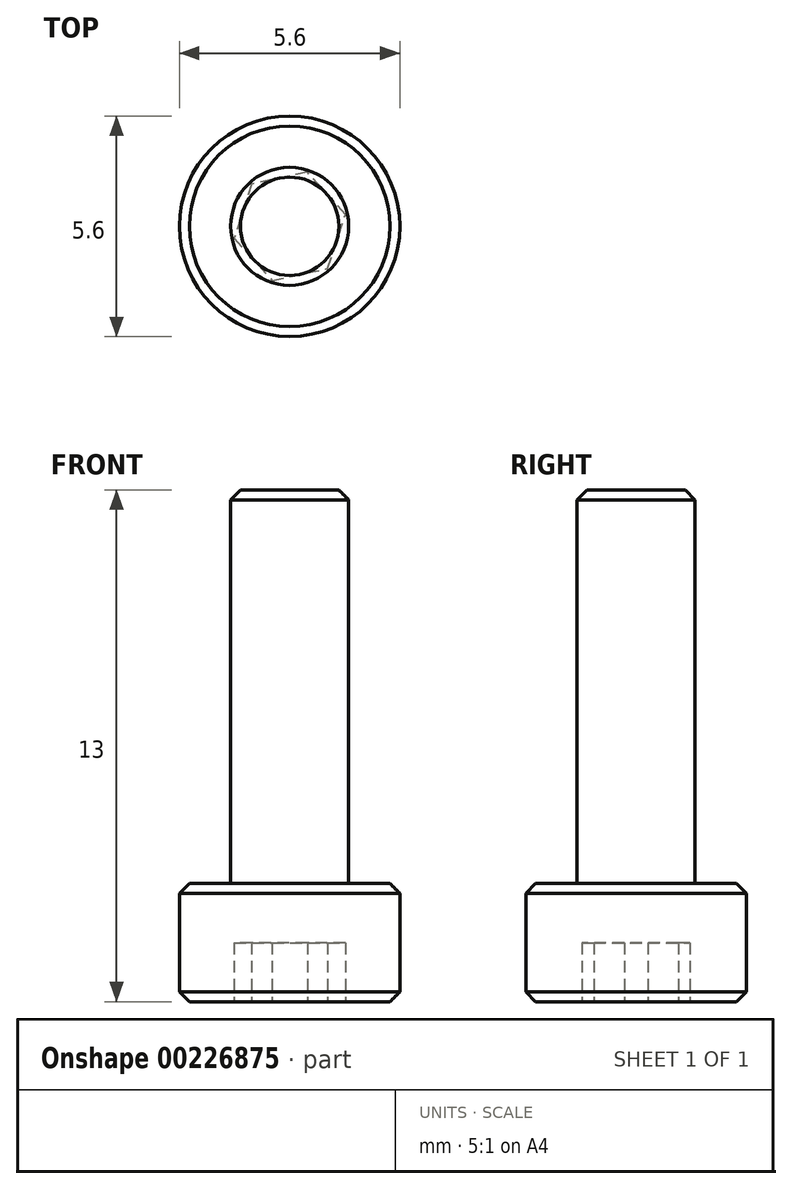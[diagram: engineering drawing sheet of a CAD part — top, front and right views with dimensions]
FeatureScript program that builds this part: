
annotation { "Feature Type Name" : "Feature", "Feature Type Description" : "" }
export const myFeature = defineFeature(function(context is Context, id is Id, definition is map)
    precondition{}
    {
        {
            var Q0;
            Q0=qCreatedBy(makeId("Top.planeOp"),FACE);
            var sketch = newSketch(context, id + "F0", { "sketchPlane" : qUnion([Q0])});
            skCircle(sketch, "E0", {"center": v(0, 0) * mm, "radius": 1.5 * mm});
            skSolve(sketch);
        }
        {
            var Q0;
            Q0 = qSketchRegion(id + "F0", true);
            extrude(context, id + "F1", {"entities" : qUnion([Q0]), "depth" : 10 * mm});
        }
        {
            var Q0;
            Q0=qCreatedBy(makeId("Top.planeOp"),FACE);
            var sketch = newSketch(context, id + "F2", { "sketchPlane" : qUnion([Q0])});
            skCircle(sketch, "E1", {"center": v(0, 0) * mm, "radius": 2.8 * mm});
            skSolve(sketch);
        }
        {
            var Q0;
            Q0 = qSketchRegion(id + "F2", true);
            extrude(context, id + "F3", {"entities" : qUnion([Q0]), "operationType" : NewBodyOperationType.ADD, "oppositeDirection" : true, "depth" : 3 * mm});
        }
        {
            var Q0;
            Q0=makeQuery(id+"F3.opExtrude","CAP_FACE",FACE,{"disambiguationData":[OSD([sQuery(id+"F2.wireOp",EDGE,"E1")])],"isStart":false});
            var sketch = newSketch(context, id + "F4", { "sketchPlane" : qUnion([Q0])});
            skCircle(sketch, "E2.cCircle", {"center": v(0, 0) * mm, "radius": 1.25 * mm, "construction": true});
            skLineSegment(sketch, "E2.0", {"start": v(1.41, -0.3) * mm, "end": v(0.45, -1.37) * mm});
            skLineSegment(sketch, "E2.1", {"start": v(0.45, -1.37) * mm, "end": v(-0.97, -1.07) * mm});
            skLineSegment(sketch, "E2.2", {"start": v(-0.97, -1.07) * mm, "end": v(-1.41, 0.3) * mm});
            skLineSegment(sketch, "E2.3", {"start": v(-1.41, 0.3) * mm, "end": v(-0.45, 1.37) * mm});
            skLineSegment(sketch, "E2.4", {"start": v(-0.45, 1.37) * mm, "end": v(0.97, 1.07) * mm});
            skLineSegment(sketch, "E2.5", {"start": v(0.97, 1.07) * mm, "end": v(1.41, -0.3) * mm});
            skPoint(sketch, "E2.0.midPoint", {"position": v(0.93, -0.84) * mm});
            skSolve(sketch);
        }
        {
            var Q0;
            Q0=makeQuery(id+"F4.imprint","IMPRINT",FACE,{"disambiguationData":[TD([[makeQuery(id+"F4.imprint","IMPRINT",EDGE,{"derivedFrom":sQuery(id+"F4.wireOp",EDGE,"E2.0")}),-1.0]])]});
            extrude(context, id + "F5", {"entities" : qUnion([Q0]), "operationType" : NewBodyOperationType.REMOVE, "oppositeDirection" : true, "depth" : 1.5 * mm});
        }
        {
            var Q0;
            Q0=makeQuery(id+"F3.opExtrude","CAP_EDGE",EDGE,{"disambiguationData":[OSD([sQuery(id+"F2.wireOp",EDGE,"E1")])],"isStart":false});
            var Q1;
            Q1=makeQuery(id+"F1.opExtrude","CAP_EDGE",EDGE,{"disambiguationData":[OSD([sQuery(id+"F0.wireOp",EDGE,"E0")])],"isStart":false});
            var Q2;
            Q2=makeQuery(id+"F3.opExtrude","CAP_EDGE",EDGE,{"disambiguationData":[OSD([sQuery(id+"F2.wireOp",EDGE,"E1")])],"isStart":true});
            chamfer(context, id + "F6", {"entities" : qUnion([Q0, Q1, Q2]), "width" : .25 * mm, "tangentPropagation" : true});
        }
    });
